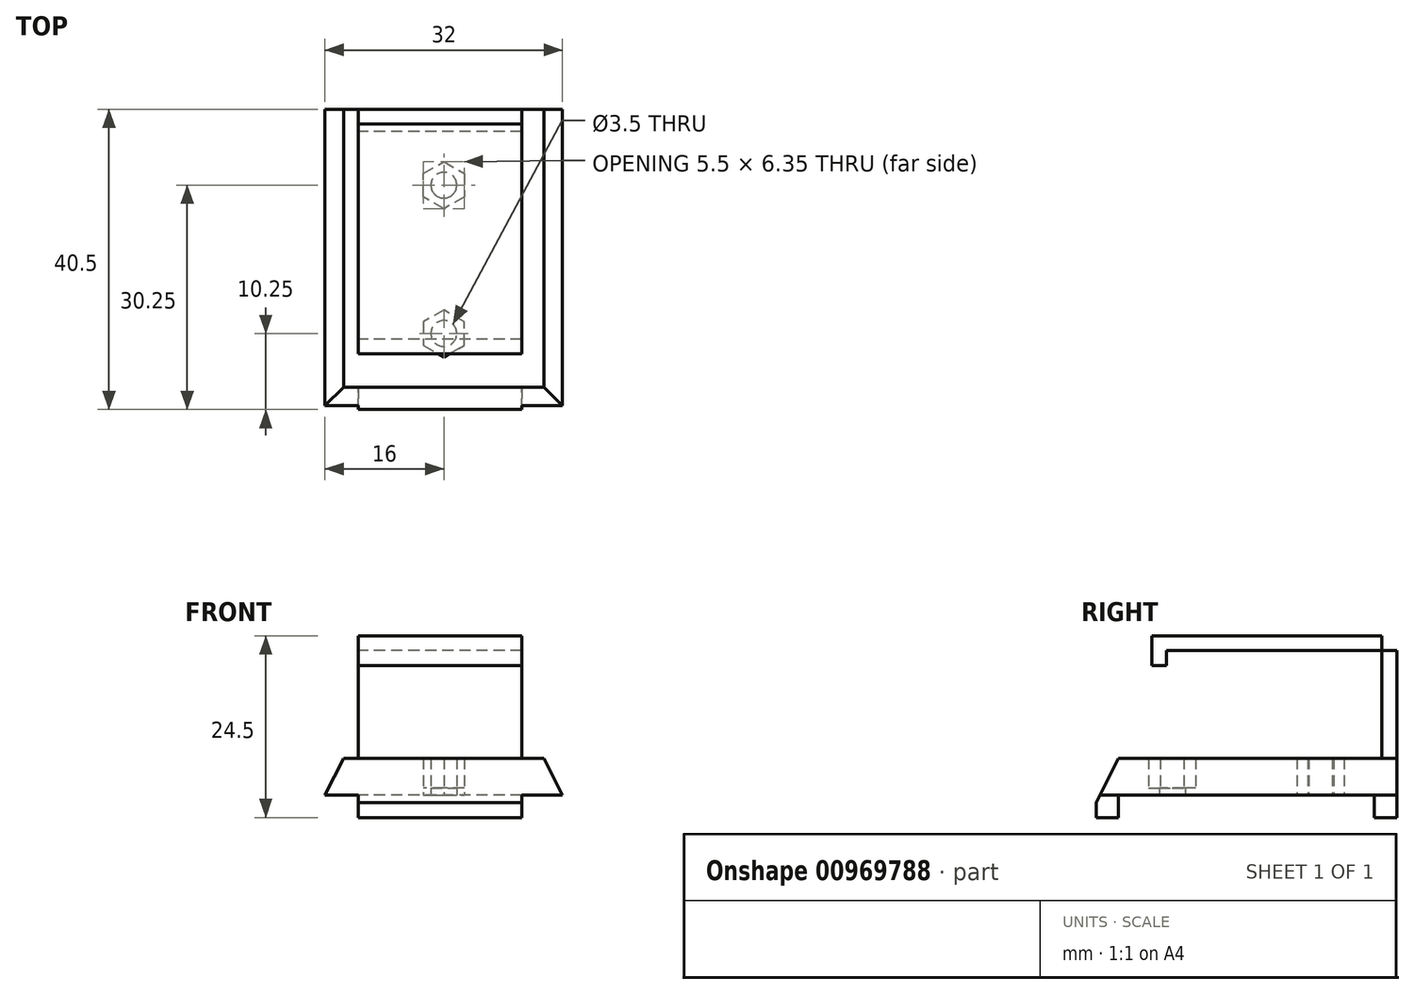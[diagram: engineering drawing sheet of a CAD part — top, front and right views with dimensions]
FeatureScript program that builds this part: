
annotation { "Feature Type Name" : "Feature", "Feature Type Description" : "" }
export const myFeature = defineFeature(function(context is Context, id is Id, definition is map)
    precondition{}
    {
        {
            var Q0;
            Q0=qCreatedBy(makeId("Right.planeOp"),FACE);
            var sketch = newSketch(context, id + "F0", { "sketchPlane" : qUnion([Q0])});
            skLineSegment(sketch, "E0.bottom", {"start": v(-20.25, 0) * mm, "end": v(-17.25, 0) * mm});
            skLineSegment(sketch, "E0.top", {"start": v(-20.25, -3) * mm, "end": v(-17.25, -3) * mm});
            skLineSegment(sketch, "E0.left", {"start": v(-20.25, 0) * mm, "end": v(-20.25, -3) * mm});
            skLineSegment(sketch, "E0.right", {"start": v(-17.25, 0) * mm, "end": v(-17.25, -3) * mm});
            skLineSegment(sketch, "E1.MirrorCS", {"start": v(17.25, 0) * mm, "end": v(17.25, -3) * mm});
            skLineSegment(sketch, "E2.MirrorCS", {"start": v(20.25, -3) * mm, "end": v(17.25, -3) * mm});
            skLineSegment(sketch, "E3.MirrorCS", {"start": v(20.25, 0) * mm, "end": v(20.25, -3) * mm});
            skLineSegment(sketch, "E4.MirrorCS", {"start": v(20.25, 0) * mm, "end": v(17.25, 0) * mm});
            skLineSegment(sketch, "E5.bottom", {"start": v(-20.25, 0) * mm, "end": v(20.25, 0) * mm});
            skLineSegment(sketch, "E5.top", {"start": v(-20.25, 5) * mm, "end": v(20.25, 5) * mm});
            skLineSegment(sketch, "E5.left", {"start": v(-20.25, 0) * mm, "end": v(-20.25, 5) * mm});
            skLineSegment(sketch, "E5.right", {"start": v(20.25, 0) * mm, "end": v(20.25, 5) * mm});
            skLineSegment(sketch, "E6.bottom", {"start": v(20.25, 5) * mm, "end": v(18.25, 5) * mm});
            skLineSegment(sketch, "E6.top", {"start": v(20.25, 21.5) * mm, "end": v(18.25, 21.5) * mm});
            skLineSegment(sketch, "E6.left", {"start": v(20.25, 5) * mm, "end": v(20.25, 21.5) * mm});
            skLineSegment(sketch, "E6.right", {"start": v(18.25, 5) * mm, "end": v(18.25, 21.5) * mm});
            skLineSegment(sketch, "E7.bottom", {"start": v(20.25, 21.5) * mm, "end": v(-10.75, 21.5) * mm});
            skLineSegment(sketch, "E7.top", {"start": v(20.25, 19.5) * mm, "end": v(-10.75, 19.5) * mm});
            skLineSegment(sketch, "E7.left", {"start": v(20.25, 19.5) * mm, "end": v(20.25, 21.5) * mm});
            skLineSegment(sketch, "E7.right", {"start": v(-10.75, 19.5) * mm, "end": v(-10.75, 21.5) * mm});
            skLineSegment(sketch, "E8.bottom", {"start": v(-10.75, 21.5) * mm, "end": v(-12.75, 21.5) * mm});
            skLineSegment(sketch, "E8.top", {"start": v(-10.75, 17.5) * mm, "end": v(-12.75, 17.5) * mm});
            skLineSegment(sketch, "E8.left", {"start": v(-10.75, 21.5) * mm, "end": v(-10.75, 17.5) * mm});
            skLineSegment(sketch, "E8.right", {"start": v(-12.75, 21.5) * mm, "end": v(-12.75, 17.5) * mm});
            skSolve(sketch);
        }
        {
            var Q0;
            Q0=makeQuery(id+"F0.imprint","IMPRINT",FACE,{"disambiguationData":[TD([[makeQuery(id+"F0.imprint","IMPRINT",EDGE,{"derivedFrom":sQuery(id+"F0.wireOp",EDGE,"E5.top")}),-1.0]])]});
            var Q1;
            Q1=makeQuery(id+"F0.imprint","IMPRINT",FACE,{"disambiguationData":[TD([[makeQuery(id+"F0.imprint","IMPRINT",EDGE,{"derivedFrom":sQuery(id+"F0.wireOp",EDGE,"E6.bottom")}),-1.0]])]});
            var Q2;
            {var subQ1=sQuery(id+"F0.wireOp",EDGE,"E7.top");Q2=makeQuery(id+"F0.imprint","IMPRINT",FACE,{"disambiguationData":[TD([[makeQuery(id+"F0.imprint","IMPRINT",EDGE,{"derivedFrom":subQ1}),1.0]])]});}
            var Q3;
            {var subQ3=sQuery(id+"F0.wireOp",EDGE,"0dvSlsed-f26J-sfsu-LQKf-inkgahWFKaY9.bottom");Q3=makeQuery(id+"F0.imprint","IMPRINT",FACE,{"disambiguationData":[TD([[makeQuery(id+"F0.imprint","IMPRINT",EDGE,{"derivedFrom":subQ3}),1.0]])]});}
            var Q4;
            Q4=makeQuery(id+"F0.imprint","IMPRINT",FACE,{"disambiguationData":[TD([[makeQuery(id+"F0.imprint","IMPRINT",EDGE,{"derivedFrom":sQuery(id+"F0.wireOp",EDGE,"E0.top")}),1.0]])]});
            var Q5;
            {var subQ0=sQuery(id+"F0.wireOp",EDGE,"E1.MirrorCS");Q5=makeQuery(id+"F0.imprint","IMPRINT",FACE,{"disambiguationData":[TD([[makeQuery(id+"F0.imprint","IMPRINT",EDGE,{"derivedFrom":subQ0}),1.0]])]});}
            var Q6;
            {var subQ0=sQuery(id+"F0.wireOp",EDGE,"E7.bottom");var subQ1=sQuery(id+"F0.wireOp",EDGE,"E6.right");var subQ2=makeQuery(id+"F0.imprint","INTERSECT",VERTEX,{"derivedFrom":[subQ1,subQ0]});Q6=makeQuery(id+"F0.imprint","IMPRINT",FACE,{"disambiguationData":[TD([[makeQuery(id+"F0.imprint","IMPRINT",EDGE,{"disambiguationData":[TD([[subQ2,1.0]])],"derivedFrom":subQ1}),1.0]])]});}
            var Q7;
            {var subQ5=sQuery(id+"F0.wireOp",EDGE,"E7.left");Q7=makeQuery(id+"F0.imprint","IMPRINT",FACE,{"disambiguationData":[TD([[makeQuery(id+"F0.imprint","IMPRINT",EDGE,{"derivedFrom":subQ5}),1.0]])]});}
            var Q8;
            {var subQ3=sQuery(id+"F0.wireOp",EDGE,"E8.bottom");Q8=makeQuery(id+"F0.imprint","IMPRINT",FACE,{"disambiguationData":[TD([[makeQuery(id+"F0.imprint","IMPRINT",EDGE,{"derivedFrom":subQ3}),1.0]])]});}
            extrude(context, id + "F1", {"entities" : qUnion([Q0, Q1, Q2, Q3, Q4, Q5, Q6, Q7, Q8]), "depth" : 22 * mm, "offsetDistance" : 25 * mm});
        }
        {
            var Q0;
            Q0=makeQuery(id+"F0.imprint","IMPRINT",FACE,{"disambiguationData":[TD([[makeQuery(id+"F0.imprint","IMPRINT",EDGE,{"derivedFrom":sQuery(id+"F0.wireOp",EDGE,"E5.top")}),-1.0]])]});
            extrude(context, id + "F2", {"entities" : qUnion([Q0]), "operationType" : NewBodyOperationType.ADD, "depth" : 28 * mm, "offsetDistance" : 25 * mm, "hasSecondDirection" : true, "secondDirectionOppositeDirection" : true, "secondDirectionDepth" : 5 * mm});
        }
        {
            var Q0;
            {var subQ0=sQuery(id+"F0.wireOp",EDGE,"E5.bottom");Q0=makeQuery(id+"F2.boolean.opBoolean","MERGE",FACE,{"derivedFrom":[makeQuery(id+"F1.opExtrude","SWEPT_FACE",FACE,{"disambiguationData":[OSD([subQ0])]}),makeQuery(id+"F2.opExtrude","SWEPT_FACE",FACE,{"disambiguationData":[OSD([subQ0])]})]});}
            var sketch = newSketch(context, id + "F3", { "sketchPlane" : qUnion([Q0])});
            skCircle(sketch, "E9.cCircle", {"center": v(11.5, 10) * mm, "radius": 2.75 * mm, "construction": true});
            skLineSegment(sketch, "E9.0", {"start": v(8.75, 8.41) * mm, "end": v(8.75, 11.59) * mm});
            skLineSegment(sketch, "E9.1", {"start": v(8.75, 11.59) * mm, "end": v(11.5, 13.18) * mm});
            skLineSegment(sketch, "E9.2", {"start": v(11.5, 13.18) * mm, "end": v(14.25, 11.59) * mm});
            skLineSegment(sketch, "E9.3", {"start": v(14.25, 11.59) * mm, "end": v(14.25, 8.41) * mm});
            skLineSegment(sketch, "E9.4", {"start": v(14.25, 8.41) * mm, "end": v(11.5, 6.82) * mm});
            skLineSegment(sketch, "E9.5", {"start": v(11.5, 6.82) * mm, "end": v(8.75, 8.41) * mm});
            skPoint(sketch, "E9.0.midPoint", {"position": v(8.75, 10) * mm});
            skLineSegment(sketch, "E10", {"start": v(11.5, 10) * mm, "end": v(-5, 10) * mm, "construction": true});
            skLineSegment(sketch, "E11", {"start": v(11.5, 10) * mm, "end": v(28, 10) * mm, "construction": true});
            skCircle(sketch, "E12", {"center": v(11.5, 10) * mm, "radius": 1.75 * mm});
            skPoint(sketch, "E13.MirrorP", {"position": v(8.75, -10) * mm});
            skLineSegment(sketch, "E14.MirrorCS", {"start": v(8.75, -11.59) * mm, "end": v(11.5, -13.18) * mm});
            skLineSegment(sketch, "E15.MirrorCS", {"start": v(11.5, -13.18) * mm, "end": v(14.25, -11.59) * mm});
            skLineSegment(sketch, "E16.MirrorCS", {"start": v(14.25, -11.59) * mm, "end": v(14.25, -8.41) * mm});
            skLineSegment(sketch, "E17.MirrorCS", {"start": v(14.25, -8.41) * mm, "end": v(11.5, -6.82) * mm});
            skCircle(sketch, "E18.MirrorC", {"center": v(11.5, -10) * mm, "radius": 1.75 * mm});
            skCircle(sketch, "E19.MirrorC", {"center": v(11.5, -10) * mm, "radius": 2.75 * mm, "construction": true});
            skLineSegment(sketch, "E20.MirrorCS", {"start": v(11.5, -6.82) * mm, "end": v(8.75, -8.41) * mm});
            skLineSegment(sketch, "E21.MirrorCS", {"start": v(8.75, -8.41) * mm, "end": v(8.75, -11.59) * mm});
            skSolve(sketch);
        }
        {
            var Q0;
            Q0=makeQuery(id+"F3.imprint","IMPRINT",FACE,{"disambiguationData":[TD([[makeQuery(id+"F3.imprint","IMPRINT",EDGE,{"derivedFrom":sQuery(id+"F3.wireOp",EDGE,"E12")}),1.0]])]});
            var Q1;
            Q1=makeQuery(id+"F3.imprint","IMPRINT",FACE,{"disambiguationData":[TD([[makeQuery(id+"F3.imprint","IMPRINT",EDGE,{"derivedFrom":sQuery(id+"F3.wireOp",EDGE,"E18.MirrorC")}),-1.0]])]});
            var Q2;
            {var subQ0=sQuery(id+"F0.wireOp",EDGE,"E5.top");Q2=makeQuery(id+"F2.boolean.opBoolean","MERGE",FACE,{"derivedFrom":[makeQuery(id+"F1.opExtrude","SWEPT_FACE",FACE,{"disambiguationData":[OSD([subQ0])]}),makeQuery(id+"F2.opExtrude","SWEPT_FACE",FACE,{"disambiguationData":[OSD([subQ0,sQuery(id+"F0.wireOp",EDGE,"E6.bottom")])]})]});}
            extrude(context, id + "F4", {"entities" : qUnion([Q0, Q1]), "operationType" : NewBodyOperationType.REMOVE, "endBound" : BoundingType.UP_TO_SURFACE, "oppositeDirection" : true, "depth" : 25 * mm, "endBoundEntityFace" : qUnion([Q2]), "offsetDistance" : 25 * mm});
        }
        {
            var Q0;
            Q0=makeQuery(id+"F3.imprint","IMPRINT",FACE,{"disambiguationData":[TD([[makeQuery(id+"F3.imprint","IMPRINT",EDGE,{"derivedFrom":sQuery(id+"F3.wireOp",EDGE,"E14.MirrorCS")}),1.0]])]});
            var Q1;
            Q1=makeQuery(id+"F3.imprint","IMPRINT",FACE,{"disambiguationData":[TD([[makeQuery(id+"F3.imprint","IMPRINT",EDGE,{"derivedFrom":sQuery(id+"F3.wireOp",EDGE,"E9.0")}),-1.0]])]});
            var Q2;
            {var subQ0=sQuery(id+"F0.wireOp",EDGE,"E5.top");Q2=makeQuery(id+"F2.boolean.opBoolean","MERGE",FACE,{"derivedFrom":[makeQuery(id+"F1.opExtrude","SWEPT_FACE",FACE,{"disambiguationData":[OSD([subQ0])]}),makeQuery(id+"F2.opExtrude","SWEPT_FACE",FACE,{"disambiguationData":[OSD([subQ0,sQuery(id+"F0.wireOp",EDGE,"E6.bottom")])]})]});}
            extrude(context, id + "F5", {"entities" : qUnion([Q0, Q1]), "operationType" : NewBodyOperationType.REMOVE, "endBound" : BoundingType.UP_TO_SURFACE, "oppositeDirection" : true, "depth" : 25 * mm, "endBoundEntityFace" : qUnion([Q2]), "offsetDistance" : 25 * mm, "hasSecondDirection" : true, "secondDirectionOppositeDirection" : true, "secondDirectionDepth" : 1 * mm});
        }
        {
            var Q0;
            Q0=makeQuery(id+"F2.opExtrude","CAP_EDGE",EDGE,{"disambiguationData":[OSD([sQuery(id+"F0.wireOp",EDGE,"E5.top"),sQuery(id+"F0.wireOp",EDGE,"E6.bottom")])],"isStart":false});
            var Q1;
            {var subQ0=sQuery(id+"F0.wireOp",EDGE,"E5.left");var subQ1=sQuery(id+"F0.wireOp",EDGE,"E5.top");Q1=makeQuery(id+"F2.boolean.opBoolean","MERGE",EDGE,{"derivedFrom":[makeQuery(id+"F1.opExtrude","SWEPT_EDGE",EDGE,{"disambiguationData":[OSD([subQ1,subQ0])]}),makeQuery(id+"F2.opExtrude","SWEPT_EDGE",EDGE,{"disambiguationData":[OSD([subQ1,subQ0])]})]});}
            var Q2;
            Q2=makeQuery(id+"F2.opExtrude","CAP_EDGE",EDGE,{"disambiguationData":[OSD([sQuery(id+"F0.wireOp",EDGE,"E5.top"),sQuery(id+"F0.wireOp",EDGE,"E6.bottom")])],"isStart":true});
            chamfer(context, id + "F6", {"entities" : qUnion([Q0, Q1, Q2]), "chamferType" : ChamferType.TWO_OFFSETS, "width1" : 3 * mm, "oppositeDirection" : false, "width2" : 6 * mm, "tangentPropagation" : true});
        }
    });
